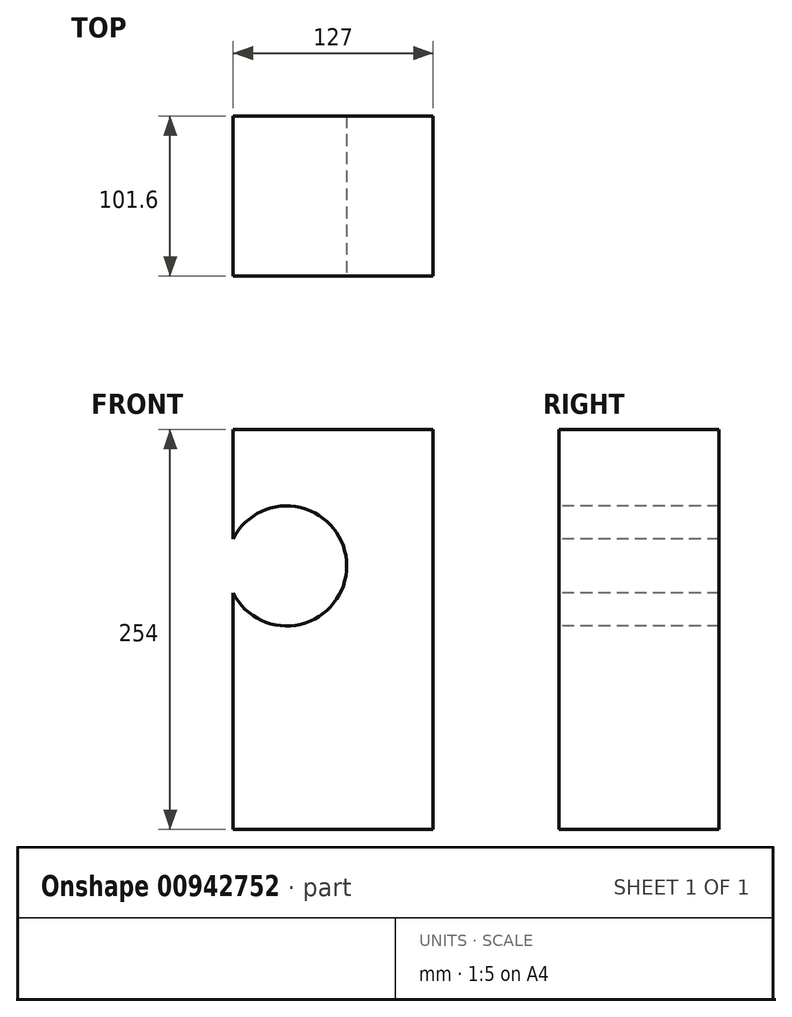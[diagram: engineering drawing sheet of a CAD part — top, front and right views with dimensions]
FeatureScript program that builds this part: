
annotation { "Feature Type Name" : "Feature", "Feature Type Description" : "" }
export const myFeature = defineFeature(function(context is Context, id is Id, definition is map)
    precondition{}
    {
        {
            var Q0;
            Q0=qCreatedBy(makeId("Front.planeOp"),FACE);
            var sketch = newSketch(context, id + "F0", { "sketchPlane" : qUnion([Q0])});
            skLineSegment(sketch, "E0.bottom", {"start": v(-133.51, 193.66) * mm, "end": v(-6.51, 193.66) * mm});
            skLineSegment(sketch, "E0.top", {"start": v(-133.51, -60.34) * mm, "end": v(-6.51, -60.34) * mm});
            skLineSegment(sketch, "E0.left", {"start": v(-133.51, 193.66) * mm, "end": v(-133.51, -60.34) * mm});
            skLineSegment(sketch, "E0.right", {"start": v(-6.51, 193.66) * mm, "end": v(-6.51, -60.34) * mm});
            skSolve(sketch);
        }
        {
            var Q0;
            Q0 = qSketchRegion(id + "F0", true);
            extrude(context, id + "F1", {"entities" : qUnion([Q0]), "depth" : 101.6 * mm, "offsetDistance" : 25.4 * mm});
        }
        {
            var Q0;
            Q0=makeQuery(id+"F1.opExtrude","CAP_FACE",FACE,{"disambiguationData":[OSD([sQuery(id+"F0.wireOp",EDGE,"E0.bottom"),sQuery(id+"F0.wireOp",EDGE,"E0.top"),sQuery(id+"F0.wireOp",EDGE,"E0.left"),sQuery(id+"F0.wireOp",EDGE,"E0.right")])],"isStart":false});
            var sketch = newSketch(context, id + "F2", { "sketchPlane" : qUnion([Q0])});
            skCircle(sketch, "E1", {"center": v(-99.52, 107.04) * mm, "radius": 38.1 * mm});
            skSolve(sketch);
        }
        {
            var Q0;
            {var subQ0=sQuery(id+"F2.wireOp",EDGE,"E1");var subQ1=makeQuery(id+"F1.opExtrude","CAP_EDGE",EDGE,{"disambiguationData":[OSD([sQuery(id+"F0.wireOp",EDGE,"E0.left")])],"isStart":false});var subQ2=makeQuery(id+"F2.imprint","INTERSECT",VERTEX,{"disambiguationData":[OD(0.0)],"derivedFrom":[subQ1,subQ0]});Q0=makeQuery(id+"F2.imprint","IMPRINT",FACE,{"disambiguationData":[TD([[makeQuery(id+"F2.imprint","IMPRINT",EDGE,{"disambiguationData":[TD([[subQ2,1.0]])],"derivedFrom":subQ0}),1.0]])]});}
            extrude(context, id + "F3", {"entities" : qUnion([Q0]), "operationType" : NewBodyOperationType.REMOVE, "endBound" : BoundingType.THROUGH_ALL, "oppositeDirection" : true, "depth" : 25.4 * mm, "offsetDistance" : 25.4 * mm});
        }
    });
